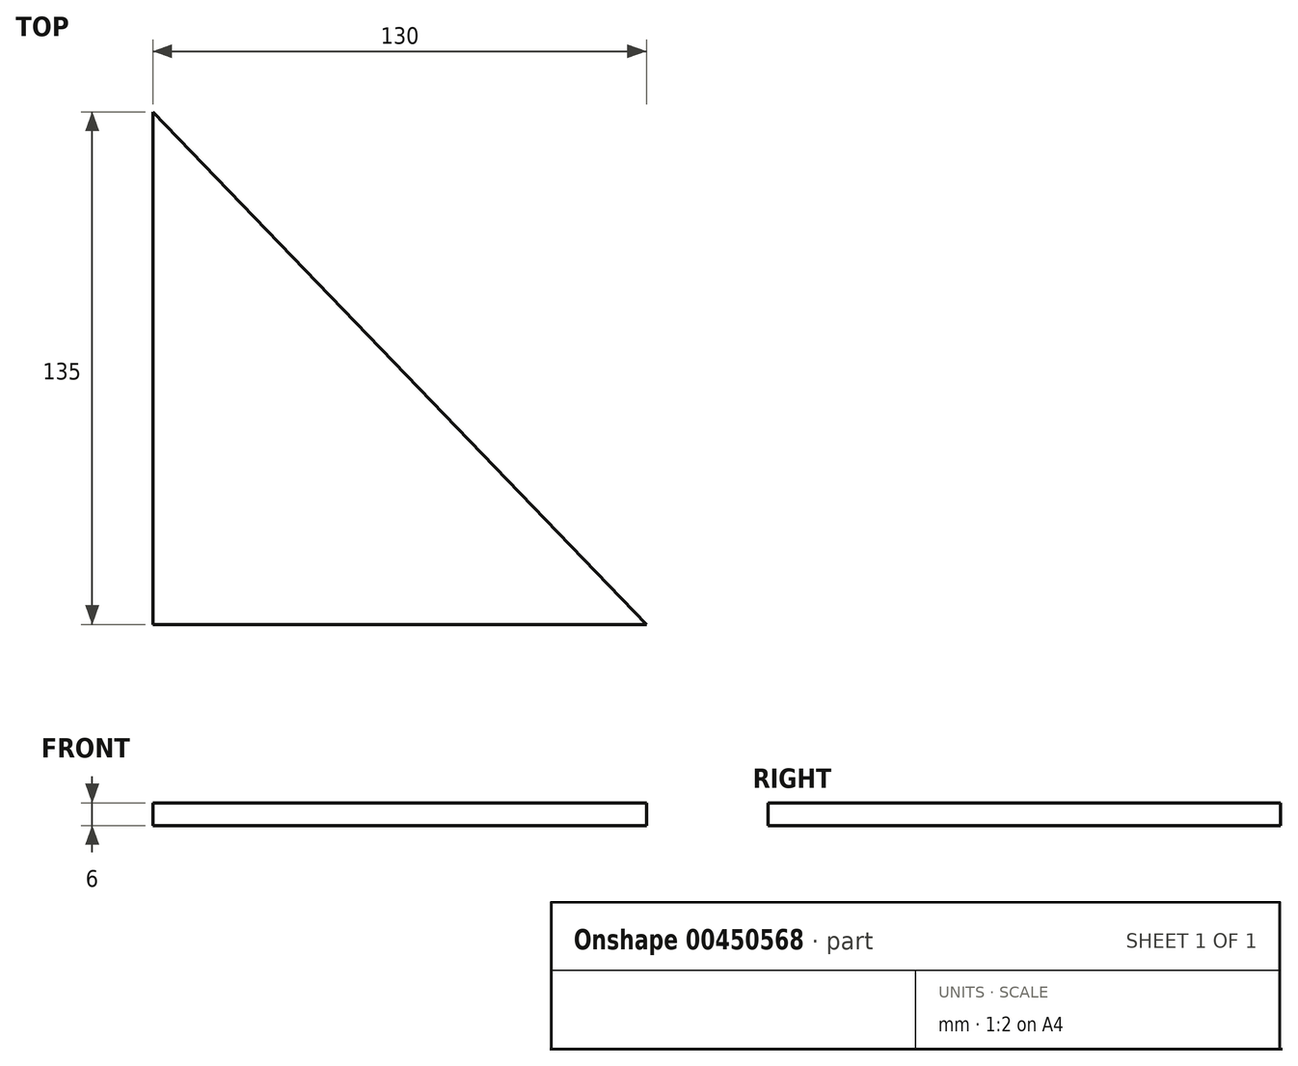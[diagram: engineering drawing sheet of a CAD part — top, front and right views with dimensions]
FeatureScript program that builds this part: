
annotation { "Feature Type Name" : "Feature", "Feature Type Description" : "" }
export const myFeature = defineFeature(function(context is Context, id is Id, definition is map)
    precondition{}
    {
        {
            var Q0;
            Q0=qCreatedBy(makeId("Top.planeOp"),FACE);
            var sketch = newSketch(context, id + "F0", { "sketchPlane" : qUnion([Q0])});
            skLineSegment(sketch, "E0", {"start": v(-28.95, 122.6) * mm, "end": v(-28.95, -12.4) * mm});
            skLineSegment(sketch, "E1", {"start": v(-28.95, -12.4) * mm, "end": v(101.05, -12.4) * mm});
            skLineSegment(sketch, "E2", {"start": v(-28.95, 122.6) * mm, "end": v(101.05, -12.4) * mm});
            skSolve(sketch);
        }
        {
            var Q0;
            Q0=makeQuery(id+"F0.imprint","IMPRINT",FACE,{"disambiguationData":[TD([[makeQuery(id+"F0.imprint","IMPRINT",EDGE,{"derivedFrom":sQuery(id+"F0.wireOp",EDGE,"E0")}),1.0]])]});
            extrude(context, id + "F1", {"entities" : qUnion([Q0]), "depth" : 6 * mm});
        }
    });
